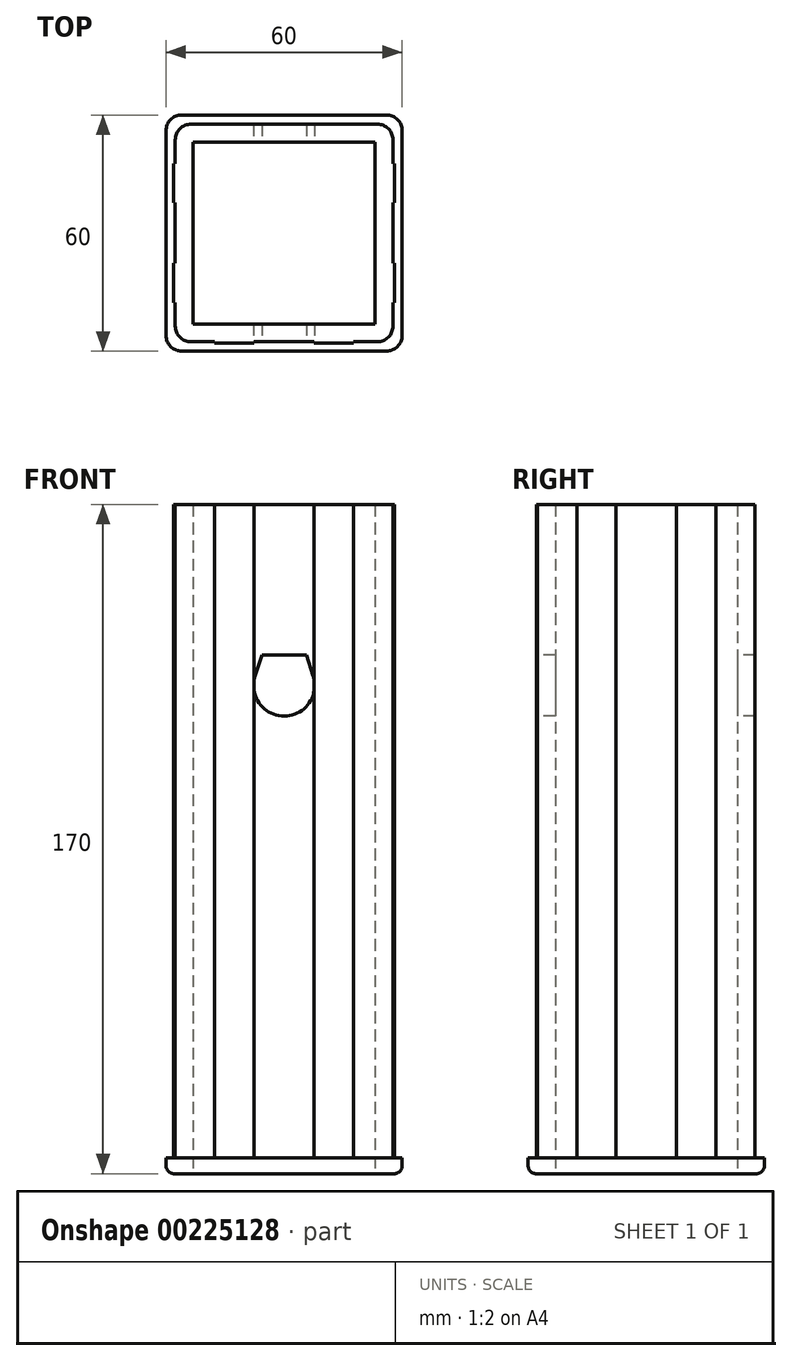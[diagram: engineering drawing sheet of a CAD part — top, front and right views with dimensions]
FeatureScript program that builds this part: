
annotation { "Feature Type Name" : "Feature", "Feature Type Description" : "" }
export const myFeature = defineFeature(function(context is Context, id is Id, definition is map)
    precondition{}
    {
        {
            var Q0;
            Q0=qCreatedBy(makeId("Top.planeOp"),FACE);
            var sketch = newSketch(context, id + "F0", { "sketchPlane" : qUnion([Q0])});
            skLineSegment(sketch, "E0.bottom", {"start": v(30, 30) * mm, "end": v(-30, 30) * mm});
            skLineSegment(sketch, "E0.top", {"start": v(30, -30) * mm, "end": v(-30, -30) * mm});
            skLineSegment(sketch, "E0.left", {"start": v(30, 30) * mm, "end": v(30, -30) * mm});
            skLineSegment(sketch, "E0.right", {"start": v(-30, 30) * mm, "end": v(-30, -30) * mm});
            skPoint(sketch, "E0.middle", {"position": v(0, 0) * mm});
            skLineSegment(sketch, "E1.bottom", {"start": v(23.1, 23.1) * mm, "end": v(-23.1, 23.1) * mm});
            skLineSegment(sketch, "E1.top", {"start": v(23.1, -23.1) * mm, "end": v(-23.1, -23.1) * mm});
            skLineSegment(sketch, "E1.left", {"start": v(23.1, 23.1) * mm, "end": v(23.1, -23.1) * mm});
            skLineSegment(sketch, "E1.right", {"start": v(-23.1, 23.1) * mm, "end": v(-23.1, -23.1) * mm});
            skLineSegment(sketch, "E2.bottom", {"start": v(27.65, 27.65) * mm, "end": v(-27.65, 27.65) * mm});
            skLineSegment(sketch, "E2.top", {"start": v(27.65, -27.65) * mm, "end": v(17.65, -27.65) * mm});
            skLineSegment(sketch, "E2.left", {"start": v(27.65, 27.65) * mm, "end": v(27.65, 17.65) * mm});
            skLineSegment(sketch, "E2.right", {"start": v(-27.65, 27.65) * mm, "end": v(-27.65, 17.65) * mm});
            skLineSegment(sketch, "E3", {"start": v(27.65, 17.65) * mm, "end": v(28.05, 17.65) * mm});
            skLineSegment(sketch, "E4", {"start": v(28.05, 17.65) * mm, "end": v(28.05, 7.65) * mm});
            skLineSegment(sketch, "E5", {"start": v(27.65, 7.65) * mm, "end": v(28.05, 7.65) * mm});
            skLineSegment(sketch, "E6.trimOffspring", {"start": v(27.65, 7.65) * mm, "end": v(27.65, -7.65) * mm});
            skLineSegment(sketch, "E7", {"start": v(27.65, -17.65) * mm, "end": v(28.05, -17.65) * mm});
            skLineSegment(sketch, "E8", {"start": v(28.05, -17.65) * mm, "end": v(28.05, -7.65) * mm});
            skLineSegment(sketch, "E9", {"start": v(28.05, -7.65) * mm, "end": v(27.65, -7.65) * mm});
            skLineSegment(sketch, "E10.trimOffspring", {"start": v(27.65, -17.65) * mm, "end": v(27.65, -27.65) * mm});
            skLineSegment(sketch, "E11", {"start": v(17.65, -27.65) * mm, "end": v(17.65, -27.95) * mm});
            skLineSegment(sketch, "E12", {"start": v(17.65, -27.95) * mm, "end": v(7.65, -27.95) * mm});
            skLineSegment(sketch, "E13", {"start": v(7.65, -27.95) * mm, "end": v(7.65, -27.65) * mm});
            skLineSegment(sketch, "E14", {"start": v(-7.65, -27.65) * mm, "end": v(-7.65, -27.95) * mm});
            skLineSegment(sketch, "E15", {"start": v(-7.65, -27.95) * mm, "end": v(-17.65, -27.95) * mm});
            skLineSegment(sketch, "E16", {"start": v(-17.65, -27.95) * mm, "end": v(-17.65, -27.65) * mm});
            skLineSegment(sketch, "E17", {"start": v(-27.65, -17.65) * mm, "end": v(-28.05, -17.65) * mm});
            skLineSegment(sketch, "E18", {"start": v(-28.05, -17.65) * mm, "end": v(-28.05, -7.65) * mm});
            skLineSegment(sketch, "E19", {"start": v(-28.05, -7.65) * mm, "end": v(-27.65, -7.65) * mm});
            skLineSegment(sketch, "E20", {"start": v(-27.65, 17.65) * mm, "end": v(-28.05, 17.65) * mm});
            skLineSegment(sketch, "E21", {"start": v(-28.05, 17.65) * mm, "end": v(-28.05, 7.65) * mm});
            skLineSegment(sketch, "E22", {"start": v(-28.05, 7.65) * mm, "end": v(-27.65, 7.65) * mm});
            skLineSegment(sketch, "E23.trimOffspring", {"start": v(-27.65, 7.65) * mm, "end": v(-27.65, -7.65) * mm});
            skLineSegment(sketch, "E24.trimOffspring", {"start": v(-27.65, -17.65) * mm, "end": v(-27.65, -27.65) * mm});
            skLineSegment(sketch, "E25.trimOffspring", {"start": v(-17.65, -27.65) * mm, "end": v(-27.65, -27.65) * mm});
            skLineSegment(sketch, "E26.trimOffspring", {"start": v(7.65, -27.65) * mm, "end": v(-7.65, -27.65) * mm});
            skSolve(sketch);
        }
        {
            var Q0;
            Q0=makeQuery(id+"F0.imprint","IMPRINT",FACE,{"disambiguationData":[TD([[makeQuery(id+"F0.imprint","IMPRINT",EDGE,{"derivedFrom":sQuery(id+"F0.wireOp",EDGE,"E1.bottom")}),-1.0]])]});
            extrude(context, id + "F1", {"entities" : qUnion([Q0]), "depth" : 166 * mm});
        }
        {
            var Q0;
            Q0=makeQuery(id+"F0.imprint","IMPRINT",FACE,{"disambiguationData":[TD([[makeQuery(id+"F0.imprint","IMPRINT",EDGE,{"derivedFrom":sQuery(id+"F0.wireOp",EDGE,"E0.bottom")}),1.0]])]});
            var Q1;
            Q1=makeQuery(id+"F0.imprint","IMPRINT",FACE,{"disambiguationData":[TD([[makeQuery(id+"F0.imprint","IMPRINT",EDGE,{"derivedFrom":sQuery(id+"F0.wireOp",EDGE,"E1.bottom")}),-1.0]])]});
            extrude(context, id + "F2", {"entities" : qUnion([Q0, Q1]), "operationType" : NewBodyOperationType.ADD, "oppositeDirection" : true, "depth" : 4 * mm});
        }
        {
            var Q0;
            Q0=makeQuery(id+"F1.opExtrude","SWEPT_EDGE",EDGE,{"disambiguationData":[OSD([sQuery(id+"F0.wireOp",EDGE,"E2.bottom"),sQuery(id+"F0.wireOp",EDGE,"E2.right")])]});
            var Q1;
            Q1=makeQuery(id+"F1.opExtrude","SWEPT_EDGE",EDGE,{"disambiguationData":[OSD([sQuery(id+"F0.wireOp",EDGE,"E24.trimOffspring"),sQuery(id+"F0.wireOp",EDGE,"E25.trimOffspring")])]});
            var Q2;
            Q2=makeQuery(id+"F1.opExtrude","SWEPT_EDGE",EDGE,{"disambiguationData":[OSD([sQuery(id+"F0.wireOp",EDGE,"E2.top"),sQuery(id+"F0.wireOp",EDGE,"E10.trimOffspring")])]});
            var Q3;
            Q3=makeQuery(id+"F1.opExtrude","SWEPT_EDGE",EDGE,{"disambiguationData":[OSD([sQuery(id+"F0.wireOp",EDGE,"E2.bottom"),sQuery(id+"F0.wireOp",EDGE,"E2.left")])]});
            var Q4;
            Q4=makeQuery(id+"F2.opExtrude","SWEPT_EDGE",EDGE,{"disambiguationData":[OSD([sQuery(id+"F0.wireOp",EDGE,"E0.bottom"),sQuery(id+"F0.wireOp",EDGE,"E0.left")])]});
            var Q5;
            Q5=makeQuery(id+"F2.opExtrude","SWEPT_EDGE",EDGE,{"disambiguationData":[OSD([sQuery(id+"F0.wireOp",EDGE,"E0.top"),sQuery(id+"F0.wireOp",EDGE,"E0.left")])]});
            var Q6;
            Q6=makeQuery(id+"F2.opExtrude","SWEPT_EDGE",EDGE,{"disambiguationData":[OSD([sQuery(id+"F0.wireOp",EDGE,"E0.bottom"),sQuery(id+"F0.wireOp",EDGE,"E0.right")])]});
            var Q7;
            Q7=makeQuery(id+"F2.opExtrude","SWEPT_EDGE",EDGE,{"disambiguationData":[OSD([sQuery(id+"F0.wireOp",EDGE,"E0.top"),sQuery(id+"F0.wireOp",EDGE,"E0.right")])]});
            fillet(context, id + "F3", {"entities" : qUnion([Q0, Q1, Q2, Q3, Q4, Q5, Q6, Q7]), "radius" : 4 * mm, "tangentPropagation" : true, "allowEdgeOverflow" : false});
        }
        {
            var Q0;
            Q0=makeQuery(id+"F2.opExtrude","CAP_EDGE",EDGE,{"disambiguationData":[OSD([sQuery(id+"F0.wireOp",EDGE,"E0.left")])],"isStart":false});
            fillet(context, id + "F4", {"entities" : qUnion([Q0]), "radius" : 2 * mm, "tangentPropagation" : true, "allowEdgeOverflow" : false});
        }
        {
            var Q0;
            Q0=qCreatedBy(makeId("Front.planeOp"),FACE);
            cPlane(context, id + "F5", {"entities" : qUnion([Q0]), "cplaneType" : CPlaneType.OFFSET, "offset" : 27.65 * mm, "width" : 150 * mm, "height" : 150 * mm});
        }
        {
            var Q0;
            Q0=qCreatedBy(id+"F5.planeOp",FACE);
            var sketch = newSketch(context, id + "F6", { "sketchPlane" : qUnion([Q0])});
            skArc(sketch, "E27", {"start": v(-7.37, 122.4) * mm, "mid": v(0, 112.25) * mm, "end": v(7.37, 122.4) * mm});
            skArc(sketch, "E28.cCircle", {"start": v(-7.37, 122.4) * mm, "mid": v(0, 112.25) * mm, "end": v(7.37, 122.4) * mm, "construction": true});
            skLineSegment(sketch, "E28.0", {"start": v(-5.63, 127.75) * mm, "end": v(5.63, 127.75) * mm});
            skLineSegment(sketch, "E28.1", {"start": v(5.63, 127.75) * mm, "end": v(7.37, 122.4) * mm});
            skLineSegment(sketch, "E28.4", {"start": v(-7.37, 122.4) * mm, "end": v(-5.63, 127.75) * mm});
            skPoint(sketch, "E28.0.midPoint", {"position": v(0, 127.75) * mm});
            skPoint(sketch, "E29.orphan", {"position": v(0, 110.42) * mm});
            skSolve(sketch);
        }
        {
            var Q0;
            Q0=makeQuery(id+"F6.imprint","IMPRINT",FACE,{"disambiguationData":[TD([[makeQuery(id+"F6.imprint","IMPRINT",EDGE,{"derivedFrom":sQuery(id+"F6.wireOp",EDGE,"E27")}),1.0]])]});
            extrude(context, id + "F7", {"entities" : qUnion([Q0]), "operationType" : NewBodyOperationType.REMOVE, "oppositeDirection" : true, "depth" : 80 * mm});
        }
    });
